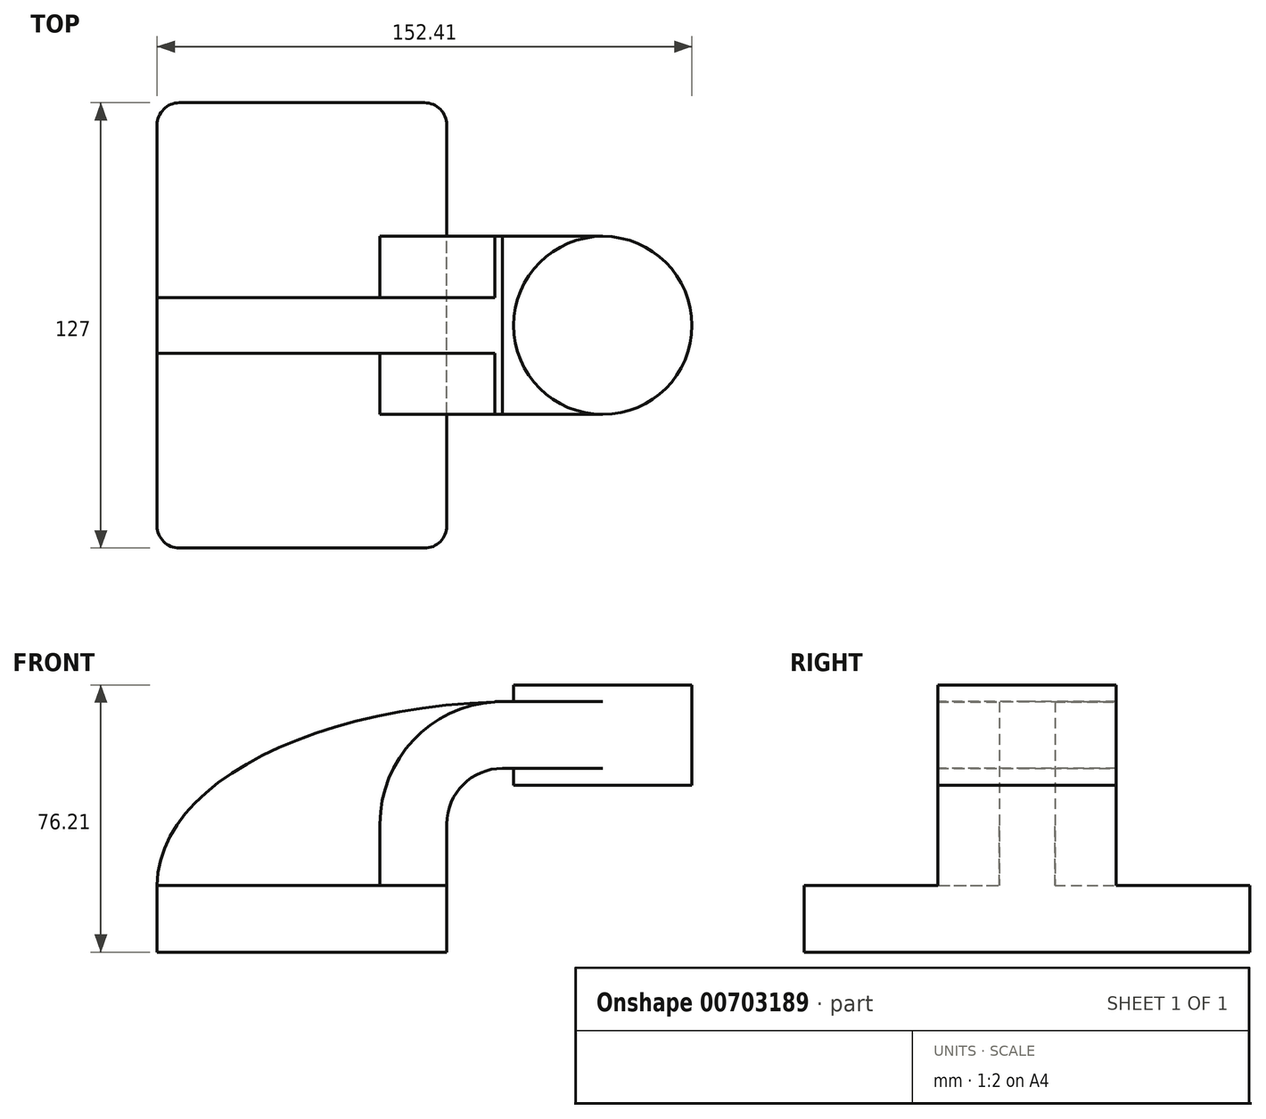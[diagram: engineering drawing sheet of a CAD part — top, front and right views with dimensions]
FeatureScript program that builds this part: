
annotation { "Feature Type Name" : "Feature", "Feature Type Description" : "" }
export const myFeature = defineFeature(function(context is Context, id is Id, definition is map)
    precondition{}
    {
        {
            var Q0;
            Q0=qCreatedBy(makeId("Front.planeOp"),FACE);
            var sketch = newSketch(context, id + "F0", { "sketchPlane" : qUnion([Q0])});
            skLineSegment(sketch, "E0.bottom", {"start": v(41.28, 9.53) * mm, "end": v(-41.28, 9.53) * mm});
            skLineSegment(sketch, "E0.top", {"start": v(41.28, -9.52) * mm, "end": v(-41.28, -9.52) * mm});
            skLineSegment(sketch, "E0.left", {"start": v(41.28, 9.53) * mm, "end": v(41.28, -9.52) * mm});
            skLineSegment(sketch, "E0.right", {"start": v(-41.28, 9.53) * mm, "end": v(-41.28, -9.52) * mm});
            skPoint(sketch, "E0.middle", {"position": v(0, 0) * mm});
            skLineSegment(sketch, "E1.bottom", {"start": v(111.12, 66.68) * mm, "end": v(60.33, 66.68) * mm});
            skLineSegment(sketch, "E1.top", {"start": v(111.12, 38.1) * mm, "end": v(60.33, 38.1) * mm});
            skLineSegment(sketch, "E1.left", {"start": v(111.13, 66.68) * mm, "end": v(111.13, 38.1) * mm});
            skLineSegment(sketch, "E1.right", {"start": v(60.33, 66.68) * mm, "end": v(60.33, 38.1) * mm});
            skPoint(sketch, "E1.middle", {"position": v(85.73, 52.39) * mm});
            skLineSegment(sketch, "E2", {"start": v(41.28, 9.53) * mm, "end": v(41.28, 27) * mm});
            skArc(sketch, "E3", {"start": v(41.27, 27) * mm, "mid": v(45.92, 38.23) * mm, "end": v(57.15, 42.88) * mm});
            skLineSegment(sketch, "E4", {"start": v(57.15, 42.88) * mm, "end": v(78.02, 42.88) * mm});
            skLineSegment(sketch, "E5", {"start": v(78.02, 42.88) * mm, "end": v(85.72, 42.88) * mm});
            skPoint(sketch, "E5.endSnap0", {"position": v(85.72, 38.1) * mm});
            skLineSegment(sketch, "E6.0", {"start": v(78.02, 61.93) * mm, "end": v(85.72, 61.93) * mm});
            skLineSegment(sketch, "E6.1", {"start": v(57.15, 61.93) * mm, "end": v(78.02, 61.93) * mm});
            skArc(sketch, "E6.2", {"start": v(22.23, 27) * mm, "mid": v(32.45, 51.7) * mm, "end": v(57.15, 61.93) * mm});
            skLineSegment(sketch, "E6.3", {"start": v(22.22, 9.53) * mm, "end": v(22.22, 27) * mm});
            skFitSpline(sketch, "E7", {"points": [v(57.15, 61.93) * mm, v(-41.28, 9.52) * mm], "startDerivative": vector(-166.87, -4.44) * mm, "endDerivative": vector(-0.05, -84.02) * mm});
            skLineSegment(sketch, "E8", {"start": v(85.72, 38.1) * mm, "end": v(85.72, 66.68) * mm});
            skSolve(sketch);
        }
        {
            var Q0;
            Q0=makeQuery(id+"F0.imprint","IMPRINT",FACE,{"disambiguationData":[TD([[makeQuery(id+"F0.imprint","IMPRINT",EDGE,{"derivedFrom":sQuery(id+"F0.wireOp",EDGE,"E0.top")}),-1.0]])]});
            extrude(context, id + "F1", {"entities" : qUnion([Q0]), "endBound" : BoundingType.SYMMETRIC, "depth" : 127 * mm, "offsetDistance" : 25.4 * mm});
        }
        {
            var Q0;
            {var subQ1=sQuery(id+"F0.wireOp",EDGE,"E2");Q0=makeQuery(id+"F0.imprint","IMPRINT",FACE,{"disambiguationData":[TD([[makeQuery(id+"F0.imprint","IMPRINT",EDGE,{"derivedFrom":subQ1}),1.0]])]});}
            var Q1;
            {var subQ1=sQuery(id+"F0.wireOp",EDGE,"E5");Q1=makeQuery(id+"F0.imprint","IMPRINT",FACE,{"disambiguationData":[TD([[makeQuery(id+"F0.imprint","IMPRINT",EDGE,{"derivedFrom":subQ1}),1.0]])]});}
            extrude(context, id + "F2", {"entities" : qUnion([Q0, Q1]), "operationType" : NewBodyOperationType.ADD, "endBound" : BoundingType.SYMMETRIC, "depth" : 50.8 * mm, "offsetDistance" : 25.4 * mm});
        }
        {
            var Q0;
            {var subQ3=sQuery(id+"F0.wireOp",EDGE,"E6.3");Q0=makeQuery(id+"F0.imprint","IMPRINT",FACE,{"disambiguationData":[TD([[makeQuery(id+"F0.imprint","IMPRINT",EDGE,{"derivedFrom":subQ3}),1.0]])]});}
            extrude(context, id + "F3", {"entities" : qUnion([Q0]), "operationType" : NewBodyOperationType.ADD, "endBound" : BoundingType.SYMMETRIC, "depth" : 15.88 * mm, "offsetDistance" : 25.4 * mm});
        }
        {
            var Q0;
            {var subQ4=sQuery(id+"F0.wireOp",EDGE,"E1.left");Q0=makeQuery(id+"F0.imprint","IMPRINT",FACE,{"disambiguationData":[TD([[makeQuery(id+"F0.imprint","IMPRINT",EDGE,{"derivedFrom":subQ4}),-1.0]])]});}
            var Q1;
            Q1=sQuery(id+"F0.wireOp",EDGE,"E8");
            revolve(context, id + "F4", {"operationType" : NewBodyOperationType.ADD, "surfaceOperationType" : NewSurfaceOperationType.NEW, "entities" : qUnion([Q0]), "axis" : qUnion([Q1]), "revolveType" : RevolveType.FULL});
        }
        {
            var Q0;
            Q0=makeQuery(id+"F1.opExtrude","CAP_EDGE",EDGE,{"disambiguationData":[OSD([sQuery(id+"F0.wireOp",EDGE,"E0.left")])],"isStart":false});
            var Q1;
            Q1=makeQuery(id+"F1.opExtrude","CAP_EDGE",EDGE,{"disambiguationData":[OSD([sQuery(id+"F0.wireOp",EDGE,"E0.right")])],"isStart":false});
            var Q2;
            Q2=makeQuery(id+"F1.opExtrude","CAP_EDGE",EDGE,{"disambiguationData":[OSD([sQuery(id+"F0.wireOp",EDGE,"E0.right")])],"isStart":true});
            var Q3;
            Q3=makeQuery(id+"F1.opExtrude","CAP_EDGE",EDGE,{"disambiguationData":[OSD([sQuery(id+"F0.wireOp",EDGE,"E0.left")])],"isStart":true});
            fillet(context, id + "F5", {"entities" : qUnion([Q0, Q1, Q2, Q3]), "radius" : 6.35 * mm, "tangentPropagation" : true, "allowEdgeOverflow" : false});
        }
    });
